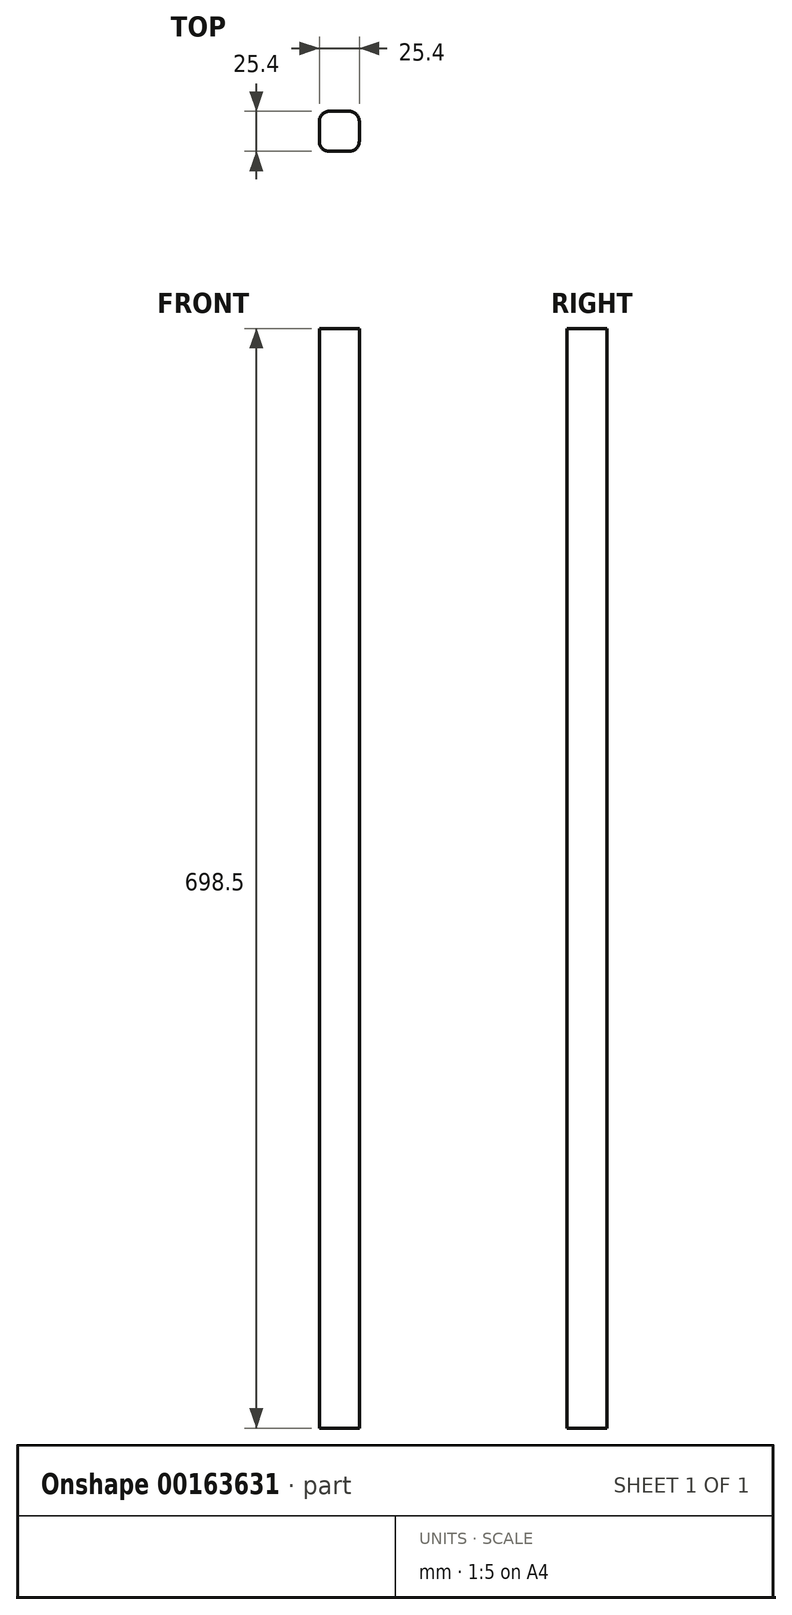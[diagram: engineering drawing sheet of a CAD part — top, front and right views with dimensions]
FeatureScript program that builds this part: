
annotation { "Feature Type Name" : "Feature", "Feature Type Description" : "" }
export const myFeature = defineFeature(function(context is Context, id is Id, definition is map)
    precondition{}
    {
        {
            var Q0;
            Q0=qCreatedBy(makeId("Top.planeOp"),FACE);
            var sketch = newSketch(context, id + "F0", { "sketchPlane" : qUnion([Q0])});
            skLineSegment(sketch, "E0.bottom", {"start": v(6.35, 12.7) * mm, "end": v(-6.35, 12.7) * mm});
            skLineSegment(sketch, "E0.top", {"start": v(6.35, -12.7) * mm, "end": v(-6.35, -12.7) * mm});
            skLineSegment(sketch, "E0.left", {"start": v(12.7, 6.35) * mm, "end": v(12.7, -6.35) * mm});
            skLineSegment(sketch, "E0.right", {"start": v(-12.7, 6.35) * mm, "end": v(-12.7, -6.35) * mm});
            skPoint(sketch, "E0.middle", {"position": v(0, 0) * mm});
            skPoint(sketch, "E1.visualSharp", {"position": v(-12.7, 12.7) * mm});
            skArc(sketch, "E1.filletArc", {"start": v(-6.35, 12.7) * mm, "mid": v(-10.84, 10.84) * mm, "end": v(-12.7, 6.35) * mm});
            skPoint(sketch, "E2.visualSharp", {"position": v(-12.7, -12.7) * mm});
            skArc(sketch, "E2.filletArc", {"start": v(-12.7, -6.35) * mm, "mid": v(-10.84, -10.84) * mm, "end": v(-6.35, -12.7) * mm});
            skPoint(sketch, "E3.visualSharp", {"position": v(12.7, -12.7) * mm});
            skArc(sketch, "E3.filletArc", {"start": v(6.35, -12.7) * mm, "mid": v(10.84, -10.84) * mm, "end": v(12.7, -6.35) * mm});
            skPoint(sketch, "E4.visualSharp", {"position": v(12.7, 12.7) * mm});
            skArc(sketch, "E4.filletArc", {"start": v(12.7, 6.35) * mm, "mid": v(10.84, 10.84) * mm, "end": v(6.35, 12.7) * mm});
            skSolve(sketch);
        }
        {
            var Q0;
            Q0=qSketchRegion(id+"F0",true);
            extrude(context, id + "F1", {"entities" : qUnion([Q0]), "depth" : 698.5 * mm, "offsetDistance" : 25.4 * mm});
        }
    });
